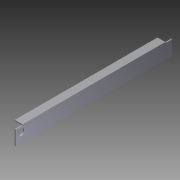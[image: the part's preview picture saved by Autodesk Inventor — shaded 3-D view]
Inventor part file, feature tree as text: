
AUTODESK INVENTOR PART (.ipt)
format: ipt  version: 2012 (Build 160160000, 160)  size: 95,744 bytes
history: native  units: in
note: dims shown in document units (in); Inventor stores cm internally (conversion verified against a paired STEP export)
features: extrude x3, sketch x3
ambient origin geometry x8: Origin, YZ Plane, XZ Plane, XY Plane, X Axis, Y Axis, Z Axis, Center Point
bodies: Solid1 (feature_tree)
feature tree (6):
  extrude  "Extrusion1"  Depth=1.0in
  extrude  "Extrusion2"  Depth=0.125in
  extrude  "Extrusion3"  Depth=0.875in
  sketch  "Sketch1"  dims[d0=2.0in d1=1.0in]
  sketch  "Sketch2"  dims[d2=0.125in d3=0.125in]
  sketch  "Sketch3"  dims[d4=20.0in d5=0.0in d6=0.875in d7=0.75in d8=0.625in d11=20.0in d12=0.0in d13=0.875in d14=0.125in d15=0.0in d16=0.875in]
